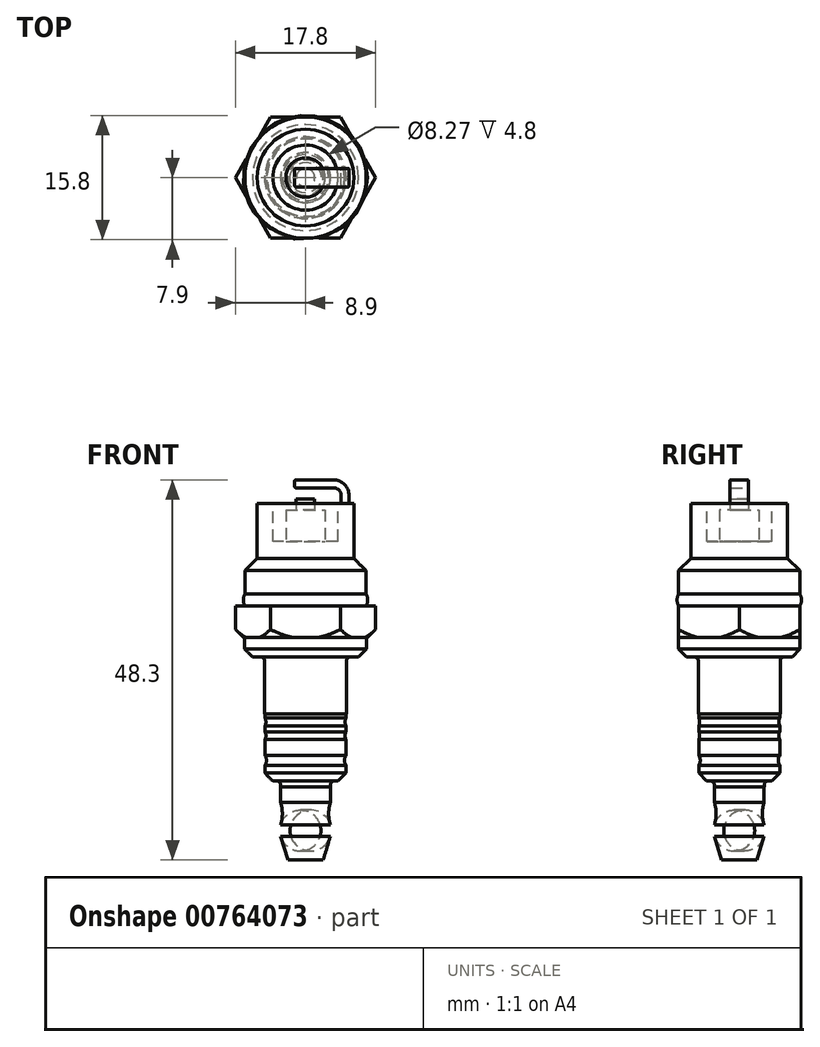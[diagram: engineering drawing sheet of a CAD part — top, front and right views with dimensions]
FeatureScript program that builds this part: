
annotation { "Feature Type Name" : "Feature", "Feature Type Description" : "" }
export const myFeature = defineFeature(function(context is Context, id is Id, definition is map)
    precondition{}
    {
        {
            var Q0;
            Q0=qCreatedBy(makeId("Front.planeOp"),FACE);
            var sketch = newSketch(context, id + "F0", { "sketchPlane" : qUnion([Q0])});
            skLineSegment(sketch, "E0", {"start": v(0, 22.65) * mm, "end": v(0, -22.65) * mm});
            skLineSegment(sketch, "E1", {"start": v(0, -22.65) * mm, "end": v(2.25, -22.65) * mm});
            skLineSegment(sketch, "E2", {"start": v(2.25, -22.65) * mm, "end": v(3.15, -19.65) * mm});
            skLineSegment(sketch, "E3", {"start": v(3.15, -18.15) * mm, "end": v(3.15, -15.35) * mm, "construction": true});
            skLineSegment(sketch, "E4", {"start": v(6.14, 22.65) * mm, "end": v(6.14, 15.65) * mm});
            skLineSegment(sketch, "E5", {"start": v(6.14, 15.65) * mm, "end": v(7.7, 14.15) * mm});
            skLineSegment(sketch, "E6", {"start": v(7.7, 14.15) * mm, "end": v(7.7, 11.15) * mm});
            skLineSegment(sketch, "E7", {"start": v(7.7, 11.15) * mm, "end": v(7.7, 9.65) * mm, "construction": true});
            skLineSegment(sketch, "E8", {"start": v(7.7, 9.65) * mm, "end": v(8.9, 9.65) * mm});
            skLineSegment(sketch, "E9", {"start": v(8.9, 9.65) * mm, "end": v(8.9, 5.65) * mm});
            skLineSegment(sketch, "E10", {"start": v(8.9, 5.65) * mm, "end": v(7.73, 5.65) * mm});
            skLineSegment(sketch, "E11", {"start": v(7.73, 5.65) * mm, "end": v(7.73, 3.15) * mm});
            skLineSegment(sketch, "E12", {"start": v(7.73, 3.15) * mm, "end": v(5.2, 3.15) * mm});
            skLineSegment(sketch, "E13", {"start": v(7.73, -1275.75) * mm, "end": v(7.53, -1275.75) * mm});
            skLineSegment(sketch, "E14", {"start": v(7.53, -408.95) * mm, "end": v(7.53, -1275.75) * mm});
            skLineSegment(sketch, "E15", {"start": v(7.53, -408.95) * mm, "end": v(7.73, -408.95) * mm});
            skLineSegment(sketch, "E16", {"start": v(7.73, -408.95) * mm, "end": v(7.73, -408.95) * mm});
            skLineSegment(sketch, "E17", {"start": v(5.2, -4.1) * mm, "end": v(5.15, -4.1) * mm});
            skLineSegment(sketch, "E18", {"start": v(5.15, -4.1) * mm, "end": v(5.15, -4.6) * mm});
            skLineSegment(sketch, "E19", {"start": v(5.15, -12.6) * mm, "end": v(3.18, -12.6) * mm});
            skLineSegment(sketch, "E20", {"start": v(3.18, -12.6) * mm, "end": v(3.18, -13.35) * mm});
            skLineSegment(sketch, "E21", {"start": v(3.18, -13.35) * mm, "end": v(3.15, -13.35) * mm});
            skLineSegment(sketch, "E22", {"start": v(3.15, -13.35) * mm, "end": v(3.15, -15.35) * mm});
            skLineSegment(sketch, "E23", {"start": v(6.14, 22.65) * mm, "end": v(4.14, 22.65) * mm});
            skLineSegment(sketch, "E24", {"start": v(4.14, 22.65) * mm, "end": v(4.14, 17.85) * mm});
            skLineSegment(sketch, "E25", {"start": v(4.14, 17.85) * mm, "end": v(0, 17.85) * mm});
            skArc(sketch, "E26", {"start": v(7.7, 9.65) * mm, "mid": v(7.9, 10.4) * mm, "end": v(7.7, 11.15) * mm});
            skPoint(sketch, "E27", {"position": v(3.15, -18.15) * mm});
            skArc(sketch, "E28", {"start": v(3.15, -19.65) * mm, "mid": v(3.26, -18.9) * mm, "end": v(3.15, -18.15) * mm});
            skArc(sketch, "E29", {"start": v(3.15, -15.35) * mm, "mid": v(2.94, -16.75) * mm, "end": v(3.15, -18.15) * mm});
            skLineSegment(sketch, "E30", {"start": v(5.2, -4.1) * mm, "end": v(5.2, 3.15) * mm});
            skLineSegment(sketch, "E31", {"start": v(5.15, -10.6) * mm, "end": v(5.15, -12.6) * mm});
            skLineSegment(sketch, "E32", {"start": v(5.15, -9.35) * mm, "end": v(5.15, -10.6) * mm, "construction": true});
            skLineSegment(sketch, "E33", {"start": v(5.15, -7.35) * mm, "end": v(5.15, -9.35) * mm});
            skLineSegment(sketch, "E34", {"start": v(5.15, -6.35) * mm, "end": v(5.15, -7.35) * mm, "construction": true});
            skLineSegment(sketch, "E35", {"start": v(5.15, -5.6) * mm, "end": v(5.15, -6.35) * mm});
            skLineSegment(sketch, "E36", {"start": v(5.15, -4.6) * mm, "end": v(5.15, -5.6) * mm, "construction": true});
            skArc(sketch, "E37", {"start": v(5.15, -9.35) * mm, "mid": v(4.96, -9.98) * mm, "end": v(5.15, -10.6) * mm});
            skArc(sketch, "E38", {"start": v(5.15, -4.6) * mm, "mid": v(5.03, -5.1) * mm, "end": v(5.15, -5.6) * mm});
            skArc(sketch, "E39", {"start": v(5.15, -6.35) * mm, "mid": v(5.03, -6.85) * mm, "end": v(5.15, -7.35) * mm});
            skSolve(sketch);
        }
        {
            var Q0;
            {var subQ1=sQuery(id+"F0.wireOp",EDGE,"E1");Q0=makeQuery(id+"F0.imprint","IMPRINT",FACE,{"disambiguationData":[TD([[makeQuery(id+"F0.imprint","IMPRINT",EDGE,{"derivedFrom":subQ1}),1.0]])]});}
            var Q1;
            Q1=sQuery(id+"F0.wireOp",EDGE,"E0");
            revolve(context, id + "F1", {"entities" : qUnion([Q0]), "axis" : qUnion([Q1]), "revolveType" : RevolveType.FULL});
        }
        {
            var Q0;
            Q0=makeQuery(id+"F1.opRevolve","SWEPT_FACE",FACE,{"disambiguationData":[OSD([sQuery(id+"F0.wireOp",EDGE,"E8")])]});
            var sketch = newSketch(context, id + "F2", { "sketchPlane" : qUnion([Q0])});
            skCircle(sketch, "E40.cCircle", {"center": v(0, 0) * mm, "radius": 7.7 * mm, "construction": true});
            skLineSegment(sketch, "E40.0", {"start": v(-4.45, 7.7) * mm, "end": v(4.45, 7.7) * mm});
            skLineSegment(sketch, "E40.1", {"start": v(4.45, 7.7) * mm, "end": v(8.9, 0) * mm});
            skLineSegment(sketch, "E40.2", {"start": v(8.9, 0) * mm, "end": v(4.45, -7.7) * mm});
            skLineSegment(sketch, "E40.3", {"start": v(4.45, -7.7) * mm, "end": v(-4.45, -7.7) * mm});
            skLineSegment(sketch, "E40.4", {"start": v(-4.45, -7.7) * mm, "end": v(-8.9, 0) * mm});
            skLineSegment(sketch, "E40.5", {"start": v(-8.9, 0) * mm, "end": v(-4.45, 7.7) * mm});
            skPoint(sketch, "E40.0.midPoint", {"position": v(0, 7.7) * mm});
            skSolve(sketch);
        }
        {
            var Q0;
            {var subQ0=sQuery(id+"F2.wireOp",EDGE,"E40.5");Q0=makeQuery(id+"F2.imprint","IMPRINT",FACE,{"disambiguationData":[TD([[makeQuery(id+"F2.imprint","IMPRINT",EDGE,{"derivedFrom":subQ0}),1.0]])]});}
            var Q1;
            {var subQ0=sQuery(id+"F2.wireOp",EDGE,"E40.4");Q1=makeQuery(id+"F2.imprint","IMPRINT",FACE,{"disambiguationData":[TD([[makeQuery(id+"F2.imprint","IMPRINT",EDGE,{"derivedFrom":subQ0}),1.0]])]});}
            var Q2;
            {var subQ0=sQuery(id+"F2.wireOp",EDGE,"E40.3");Q2=makeQuery(id+"F2.imprint","IMPRINT",FACE,{"disambiguationData":[TD([[makeQuery(id+"F2.imprint","IMPRINT",EDGE,{"derivedFrom":subQ0}),1.0]])]});}
            var Q3;
            {var subQ0=sQuery(id+"F2.wireOp",EDGE,"E40.2");Q3=makeQuery(id+"F2.imprint","IMPRINT",FACE,{"disambiguationData":[TD([[makeQuery(id+"F2.imprint","IMPRINT",EDGE,{"derivedFrom":subQ0}),1.0]])]});}
            var Q4;
            {var subQ0=sQuery(id+"F2.wireOp",EDGE,"E40.1");Q4=makeQuery(id+"F2.imprint","IMPRINT",FACE,{"disambiguationData":[TD([[makeQuery(id+"F2.imprint","IMPRINT",EDGE,{"derivedFrom":subQ0}),1.0]])]});}
            var Q5;
            {var subQ0=sQuery(id+"F2.wireOp",EDGE,"E40.0");Q5=makeQuery(id+"F2.imprint","IMPRINT",FACE,{"disambiguationData":[TD([[makeQuery(id+"F2.imprint","IMPRINT",EDGE,{"derivedFrom":subQ0}),1.0]])]});}
            var Q6;
            Q6=makeQuery(id+"F1.opRevolve","SWEPT_FACE",FACE,{"disambiguationData":[OSD([sQuery(id+"F0.wireOp",EDGE,"E10")])]});
            extrude(context, id + "F3", {"entities" : qUnion([Q0, Q1, Q2, Q3, Q4, Q5]), "operationType" : NewBodyOperationType.REMOVE, "endBound" : BoundingType.UP_TO_SURFACE, "oppositeDirection" : true, "endBoundEntityFace" : qUnion([Q6]), "depth" : 25 * mm});
        }
        {
            var Q0;
            Q0=makeQuery(id+"F1.opRevolve","SWEPT_FACE",FACE,{"disambiguationData":[OSD([sQuery(id+"F0.wireOp",EDGE,"E25")])]});
            var sketch = newSketch(context, id + "F4", { "sketchPlane" : qUnion([Q0])});
            skCircle(sketch, "E41", {"center": v(0, 0) * mm, "radius": 2.5 * mm});
            skCircle(sketch, "E42", {"center": v(0, 0) * mm, "radius": 1.18 * mm});
            skSolve(sketch);
        }
        {
            var Q0;
            Q0=makeQuery(id+"F4.imprint","IMPRINT",FACE,{"disambiguationData":[TD([[makeQuery(id+"F4.imprint","IMPRINT",EDGE,{"derivedFrom":sQuery(id+"F4.wireOp",EDGE,"E41")}),1.0]])]});
            extrude(context, id + "F5", {"entities" : qUnion([Q0]), "operationType" : NewBodyOperationType.ADD, "depth" : 4 * mm});
        }
        {
            var Q0;
            Q0=makeQuery(id+"F5.boolean.opBoolean","SPLIT",FACE,{"disambiguationData":[TD([makeQuery(id+"F5.opExtrude","SWEPT_FACE",FACE,{"disambiguationData":[OSD([sQuery(id+"F4.wireOp",EDGE,"E42")])]})])],"derivedFrom":makeQuery(id+"F1.opRevolve","SWEPT_FACE",FACE,{"disambiguationData":[OSD([sQuery(id+"F0.wireOp",EDGE,"E25")])]})});
            extrude(context, id + "F6", {"entities" : qUnion([Q0]), "operationType" : NewBodyOperationType.ADD, "depth" : 5.35 * mm});
        }
        {
            var Q0;
            Q0=makeQuery(id+"F1.opRevolve","SWEPT_EDGE",EDGE,{"disambiguationData":[OSD([sQuery(id+"F0.wireOp",EDGE,"E11"),sQuery(id+"F0.wireOp",EDGE,"E12")])]});
            var Q1;
            Q1=makeQuery(id+"F1.opRevolve","SWEPT_EDGE",EDGE,{"disambiguationData":[OSD([sQuery(id+"F0.wireOp",EDGE,"E19"),sQuery(id+"F0.wireOp",EDGE,"E31")])]});
            chamfer(context, id + "F7", {"entities" : qUnion([Q0, Q1]), "width" : 1 * mm, "tangentPropagation" : true});
        }
        {
            var Q0;
            Q0=qCreatedBy(makeId("Front.planeOp"),FACE);
            var sketch = newSketch(context, id + "F8", { "sketchPlane" : qUnion([Q0])});
            skLineSegment(sketch, "E43.0", {"start": v(8.9, 5.65) * mm, "end": v(7.9, 5.65) * mm});
            skLineSegment(sketch, "E43.1", {"start": v(8.9, 5.65) * mm, "end": v(8.9, 6.65) * mm});
            skLineSegment(sketch, "E44", {"start": v(7.9, 5.65) * mm, "end": v(8.9, 6.65) * mm});
            skPoint(sketch, "E45.orphan", {"position": v(8.9, 9.65) * mm});
            skPoint(sketch, "E46.orphan", {"position": v(6.93, 5.65) * mm});
            skSolve(sketch);
        }
        {
            var Q0;
            Q0=makeQuery(id+"F8.imprint","IMPRINT",FACE,{"disambiguationData":[TD([[makeQuery(id+"F8.imprint","IMPRINT",EDGE,{"derivedFrom":sQuery(id+"F8.wireOp",EDGE,"E43.0")}),-1.0]])]});
            var Q1;
            Q1=sQuery(id+"F0.wireOp",EDGE,"E0");
            revolve(context, id + "F9", {"operationType" : NewBodyOperationType.REMOVE, "entities" : qUnion([Q0]), "axis" : qUnion([Q1]), "revolveType" : RevolveType.FULL, "oppositeDirection" : true});
        }
        {
            var Q0;
            Q0=qCreatedBy(makeId("Front.planeOp"),FACE);
            var sketch = newSketch(context, id + "F10", { "sketchPlane" : qUnion([Q0])});
            skLineSegment(sketch, "E47", {"start": v(-1.36, 25.65) * mm, "end": v(5.54, 25.65) * mm});
            skLineSegment(sketch, "E48", {"start": v(5.54, 25.65) * mm, "end": v(5.54, 22.65) * mm});
            skLineSegment(sketch, "E49", {"start": v(5.54, 22.65) * mm, "end": v(4.54, 22.65) * mm});
            skLineSegment(sketch, "E50.0", {"start": v(4.54, 24.65) * mm, "end": v(4.54, 22.65) * mm});
            skLineSegment(sketch, "E50.1", {"start": v(-1.36, 24.65) * mm, "end": v(4.54, 24.65) * mm});
            skLineSegment(sketch, "E51", {"start": v(-1.36, 25.65) * mm, "end": v(-1.36, 24.65) * mm});
            skSolve(sketch);
        }
        {
            var Q0;
            Q0=makeQuery(id+"F10.imprint","IMPRINT",FACE,{"disambiguationData":[TD([[makeQuery(id+"F10.imprint","IMPRINT",EDGE,{"derivedFrom":sQuery(id+"F10.wireOp",EDGE,"E47")}),-1.0]])]});
            extrude(context, id + "F11", {"entities" : qUnion([Q0]), "operationType" : NewBodyOperationType.ADD, "endBound" : BoundingType.SYMMETRIC, "depth" : 2.35 * mm});
        }
        {
            var Q0;
            Q0=makeQuery(id+"F11.opExtrude","SWEPT_EDGE",EDGE,{"disambiguationData":[OSD([sQuery(id+"F10.wireOp",EDGE,"E50.0"),sQuery(id+"F10.wireOp",EDGE,"E50.1")])]});
            fillet(context, id + "F12", {"entities" : qUnion([Q0]), "radius" : 1 * mm, "tangentPropagation" : true, "allowEdgeOverflow" : false});
        }
        {
            var Q0;
            Q0=makeQuery(id+"F11.opExtrude","SWEPT_EDGE",EDGE,{"disambiguationData":[OSD([sQuery(id+"F10.wireOp",EDGE,"E47"),sQuery(id+"F10.wireOp",EDGE,"E48")])]});
            fillet(context, id + "F13", {"entities" : qUnion([Q0]), "radius" : 2 * mm, "tangentPropagation" : true, "allowEdgeOverflow" : false});
        }
        {
            var Q0;
            Q0=makeQuery(id+"F11.opExtrude","CAP_FACE",FACE,{"disambiguationData":[OSD([sQuery(id+"F10.wireOp",EDGE,"E47"),sQuery(id+"F10.wireOp",EDGE,"E48"),sQuery(id+"F10.wireOp",EDGE,"E49"),sQuery(id+"F10.wireOp",EDGE,"E50.0"),sQuery(id+"F10.wireOp",EDGE,"E50.1"),sQuery(id+"F10.wireOp",EDGE,"E51")])],"isStart":false});
            var Q1;
            Q1=makeQuery(id+"F11.opExtrude","SWEPT_FACE",FACE,{"disambiguationData":[OSD([sQuery(id+"F10.wireOp",EDGE,"E51")])]});
            var Q2;
            Q2=makeQuery(id+"F11.opExtrude","CAP_FACE",FACE,{"disambiguationData":[OSD([sQuery(id+"F10.wireOp",EDGE,"E47"),sQuery(id+"F10.wireOp",EDGE,"E48"),sQuery(id+"F10.wireOp",EDGE,"E49"),sQuery(id+"F10.wireOp",EDGE,"E50.0"),sQuery(id+"F10.wireOp",EDGE,"E50.1"),sQuery(id+"F10.wireOp",EDGE,"E51")])],"isStart":true});
            fillet(context, id + "F14", {"entities" : qUnion([Q0, Q1, Q2]), "radius" : 0.1 * mm, "tangentPropagation" : true, "allowEdgeOverflow" : false});
        }
        {
            var Q0;
            Q0=makeQuery(id+"F1.opRevolve","SWEPT_EDGE",EDGE,{"disambiguationData":[OSD([sQuery(id+"F0.wireOp",EDGE,"E12"),sQuery(id+"F0.wireOp",EDGE,"E30")])]});
            var Q1;
            Q1=makeQuery(id+"F1.opRevolve","SWEPT_EDGE",EDGE,{"disambiguationData":[OSD([sQuery(id+"F0.wireOp",EDGE,"E19"),sQuery(id+"F0.wireOp",EDGE,"E20")])]});
            fillet(context, id + "F15", {"entities" : qUnion([Q0, Q1]), "radius" : 0.5 * mm, "tangentPropagation" : true, "allowEdgeOverflow" : false});
        }
    });
